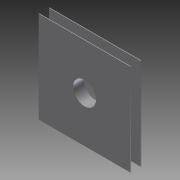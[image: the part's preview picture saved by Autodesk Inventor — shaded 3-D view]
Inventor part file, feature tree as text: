
AUTODESK INVENTOR PART (.ipt)
format: ipt  version: 2011 (Build 150239000, 239)  size: 113,664 bytes
history: native  units: in
note: dims shown in document units (in); Inventor stores cm internally (conversion verified against a paired STEP export)
features: extrude x6, sketch x6
ambient origin geometry x8: Origin, YZ Plane, XZ Plane, XY Plane, X Axis, Y Axis, Z Axis, Center Point
bodies: Solid1 (feature_tree)
feature tree (12):
  extrude  "Extrusion1"  Depth=4.0in
  extrude  "Extrusion2"  Depth=0.32in TaperAngle=0.0deg
  extrude  "Extrusion3"  Depth=0.32in TaperAngle=0.0deg
  extrude  "Extrusion4"  Depth=0.03in
  extrude  "Extrusion5"  Depth=1.5in
  extrude  "Extrusion6"  Depth=1.0in TaperAngle=0.0deg
  sketch  "Sketch1"  dims[d0=4.0in d1=4.0in]
  sketch  "Sketch2"  dims[d2=1.0in d3=0.32in d4=0.155in d5=0.0in d6=0.0in]
  sketch  "Sketch3"  dims[d7=1.0in d8=0.32in d9=0.0in]
  sketch  "Sketch4"  dims[d10=0.03in d11=0.03in]
  sketch  "Sketch5"  dims[d12=4.0in d13=0.0in d14=1.5in]
  sketch  "Sketch6"  dims[d15=0.32in d16=0.0in d17=1.0in d18=0.0in d19=0.14in d20=0.0in]
